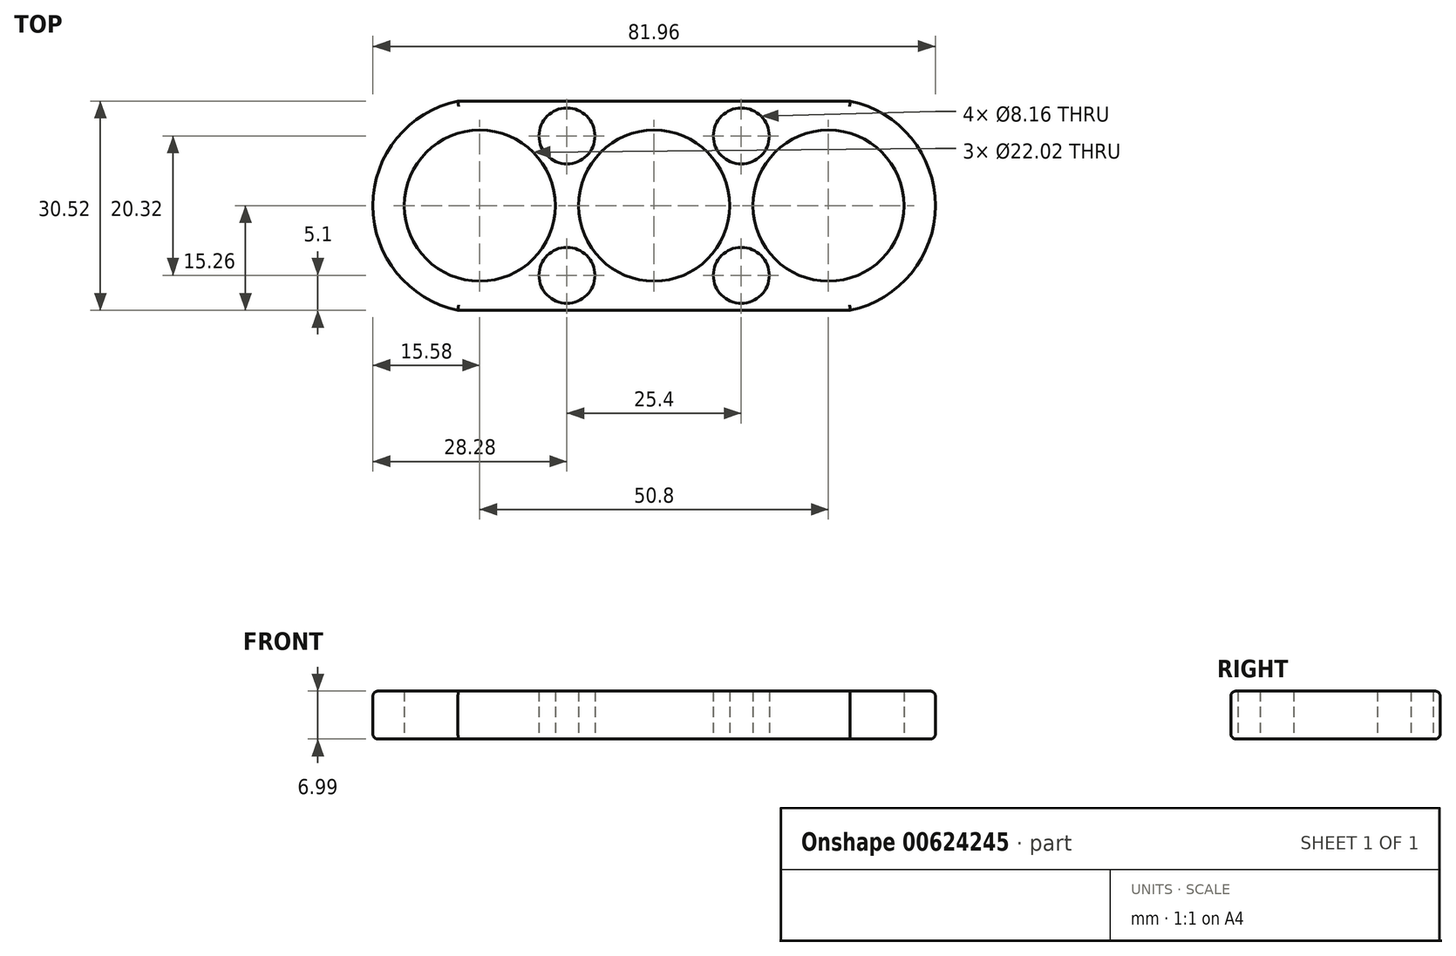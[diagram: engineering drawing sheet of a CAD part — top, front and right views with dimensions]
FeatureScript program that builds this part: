
annotation { "Feature Type Name" : "Feature", "Feature Type Description" : "" }
export const myFeature = defineFeature(function(context is Context, id is Id, definition is map)
    precondition{}
    {
        {
            var Q0;
            Q0=qCreatedBy(makeId("Top.planeOp"),FACE);
            var sketch = newSketch(context, id + "F0", { "sketchPlane" : qUnion([Q0])});
            skCircle(sketch, "E0", {"center": v(0, 0) * mm, "radius": 11.01 * mm});
            skLineSegment(sketch, "E1", {"start": v(0, 0) * mm, "end": v(-25.4, 0) * mm});
            skLineSegment(sketch, "E2", {"start": v(0, 0) * mm, "end": v(25.4, 0) * mm});
            skCircle(sketch, "E3", {"center": v(25.4, 0) * mm, "radius": 11.01 * mm});
            skCircle(sketch, "E4", {"center": v(-25.4, 0) * mm, "radius": 11.01 * mm});
            skArc(sketch, "E5", {"start": v(-28.58, 15.26) * mm, "mid": v(-40.98, 0) * mm, "end": v(-28.57, -15.26) * mm});
            skArc(sketch, "E6", {"start": v(28.58, -15.26) * mm, "mid": v(40.98, 0) * mm, "end": v(28.57, 15.26) * mm});
            skLineSegment(sketch, "E7", {"start": v(-28.58, 15.26) * mm, "end": v(28.58, 15.26) * mm});
            skLineSegment(sketch, "E8", {"start": v(-28.57, -15.26) * mm, "end": v(28.58, -15.26) * mm});
            skCircle(sketch, "E9", {"center": v(-12.7, 10.16) * mm, "radius": 4.08 * mm});
            skCircle(sketch, "E10", {"center": v(12.7, 10.16) * mm, "radius": 4.08 * mm});
            skCircle(sketch, "E11", {"center": v(12.7, -10.16) * mm, "radius": 4.08 * mm});
            skCircle(sketch, "E12", {"center": v(-12.7, -10.16) * mm, "radius": 4.08 * mm});
            skPoint(sketch, "E13", {"position": v(-12.7, 0) * mm});
            skPoint(sketch, "E14", {"position": v(12.7, 0) * mm});
            skSolve(sketch);
        }
        {
            var Q0;
            Q0 = qSketchRegion(id + "F0", true);
            extrude(context, id + "F1", {"entities" : qUnion([Q0]), "depth" : 7 * mm, "offsetDistance" : 25.4 * mm});
        }
        {
            var Q0;
            Q0=makeQuery(id+"F1.opExtrude","CAP_EDGE",EDGE,{"disambiguationData":[OSD([sQuery(id+"F0.wireOp",EDGE,"E5")])],"isStart":false});
            var Q1;
            Q1=makeQuery(id+"F1.opExtrude","CAP_EDGE",EDGE,{"disambiguationData":[OSD([sQuery(id+"F0.wireOp",EDGE,"E8")])],"isStart":false});
            var Q2;
            Q2=makeQuery(id+"F1.opExtrude","CAP_EDGE",EDGE,{"disambiguationData":[OSD([sQuery(id+"F0.wireOp",EDGE,"E6")])],"isStart":false});
            var Q3;
            Q3=makeQuery(id+"F1.opExtrude","CAP_EDGE",EDGE,{"disambiguationData":[OSD([sQuery(id+"F0.wireOp",EDGE,"E7")])],"isStart":false});
            fillet(context, id + "F2", {"entities" : qUnion([Q0, Q1, Q2, Q3]), "radius" : 0.76 * mm, "tangentPropagation" : true, "allowEdgeOverflow" : false});
        }
        {
            var Q0;
            Q0=makeQuery(id+"F1.opExtrude","CAP_EDGE",EDGE,{"disambiguationData":[OSD([sQuery(id+"F0.wireOp",EDGE,"E5")])],"isStart":true});
            var Q1;
            Q1=makeQuery(id+"F1.opExtrude","CAP_EDGE",EDGE,{"disambiguationData":[OSD([sQuery(id+"F0.wireOp",EDGE,"E7")])],"isStart":true});
            var Q2;
            Q2=makeQuery(id+"F1.opExtrude","CAP_EDGE",EDGE,{"disambiguationData":[OSD([sQuery(id+"F0.wireOp",EDGE,"E8")])],"isStart":true});
            var Q3;
            Q3=makeQuery(id+"F1.opExtrude","CAP_EDGE",EDGE,{"disambiguationData":[OSD([sQuery(id+"F0.wireOp",EDGE,"E6")])],"isStart":true});
            fillet(context, id + "F3", {"entities" : qUnion([Q0, Q1, Q2, Q3]), "radius" : 0.76 * mm, "tangentPropagation" : true, "allowEdgeOverflow" : false});
        }
    });
